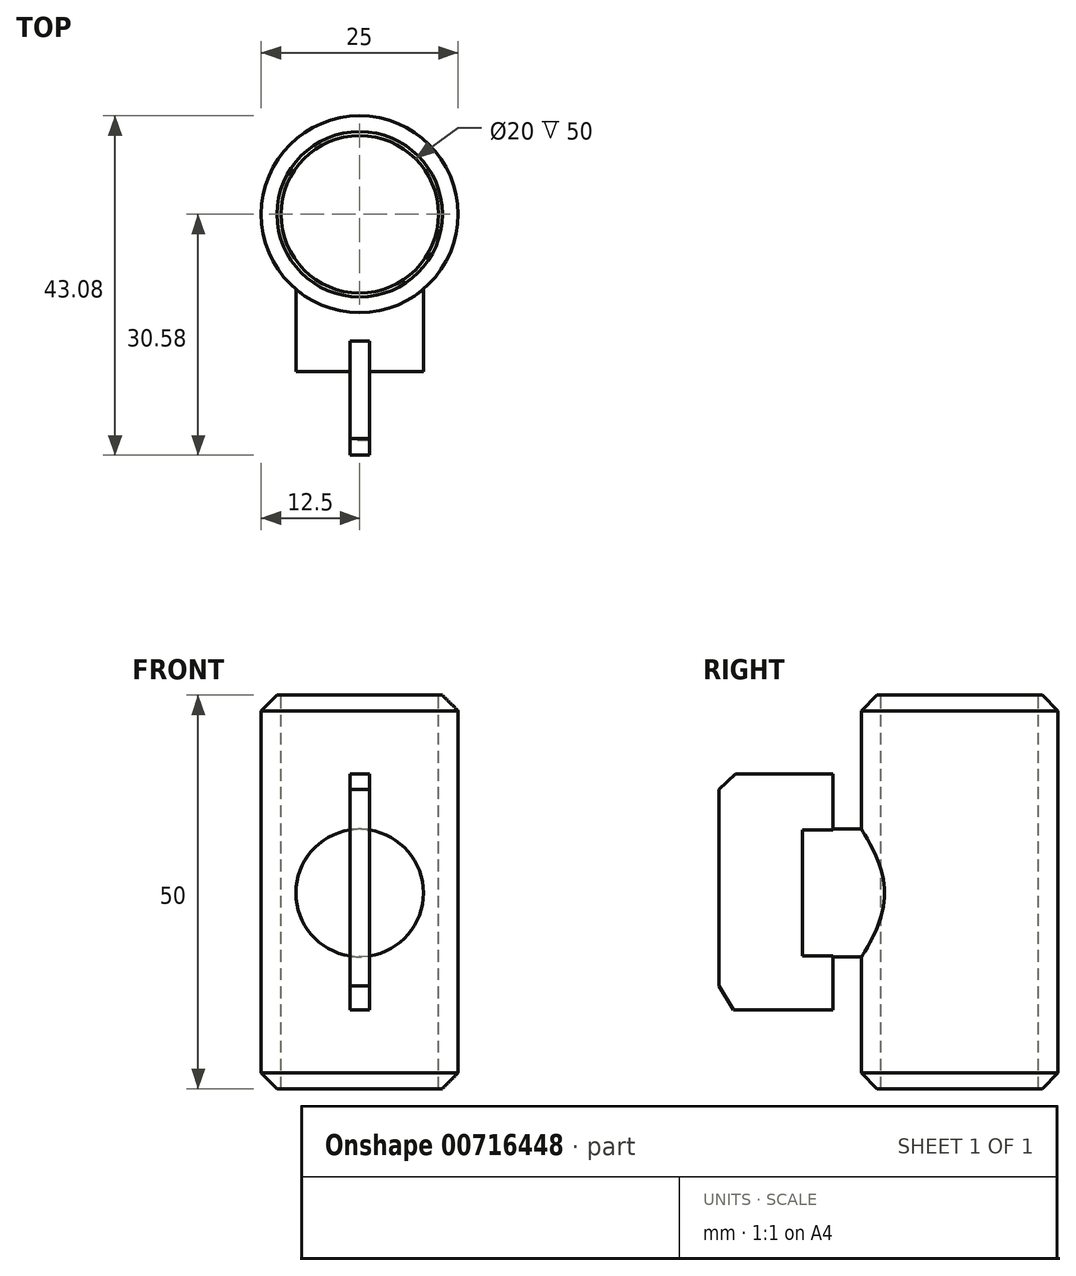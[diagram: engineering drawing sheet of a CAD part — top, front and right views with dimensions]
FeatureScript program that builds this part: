
annotation { "Feature Type Name" : "Feature", "Feature Type Description" : "" }
export const myFeature = defineFeature(function(context is Context, id is Id, definition is map)
    precondition{}
    {
        {
            var Q0;
            Q0=qCreatedBy(makeId("Top.planeOp"),FACE);
            var sketch = newSketch(context, id + "F0", { "sketchPlane" : qUnion([Q0])});
            skCircle(sketch, "E0", {"center": v(0, 0) * mm, "radius": 12.5 * mm});
            skSolve(sketch);
        }
        {
            var Q0;
            Q0=qSketchRegion(id+"F0",true);
            extrude(context, id + "F1", {"entities" : qUnion([Q0]), "depth" : 50 * mm, "offsetDistance" : 25 * mm});
        }
        {
            var Q0;
            Q0=makeQuery(id+"F1.opExtrude","CAP_EDGE",EDGE,{"disambiguationData":[OSD([sQuery(id+"F0.wireOp",EDGE,"E0")])],"isStart":false});
            var Q1;
            Q1=makeQuery(id+"F1.opExtrude","CAP_EDGE",EDGE,{"disambiguationData":[OSD([sQuery(id+"F0.wireOp",EDGE,"E0")])],"isStart":true});
            chamfer(context, id + "F2", {"entities" : qUnion([Q0, Q1]), "width" : 2 * mm, "tangentPropagation" : true});
        }
        {
            var Q0;
            Q0=qCreatedBy(makeId("Front.planeOp"),FACE);
            var sketch = newSketch(context, id + "F3", { "sketchPlane" : qUnion([Q0])});
            skCircle(sketch, "E1", {"center": v(0, 24.86) * mm, "radius": 8.1 * mm});
            skSolve(sketch);
        }
        {
            var Q0;
            Q0=qSketchRegion(id+"F3",true);
            extrude(context, id + "F4", {"entities" : qUnion([Q0]), "operationType" : NewBodyOperationType.ADD, "depth" : 20 * mm, "offsetDistance" : 25 * mm});
        }
        {
            var Q0;
            Q0=makeQuery(id+"F1.opExtrude","CAP_FACE",FACE,{"disambiguationData":[OSD([sQuery(id+"F0.wireOp",EDGE,"E0")])],"isStart":false});
            var sketch = newSketch(context, id + "F5", { "sketchPlane" : qUnion([Q0])});
            skCircle(sketch, "E2", {"center": v(0, 0) * mm, "radius": 10 * mm});
            skSolve(sketch);
        }
        {
            var Q0;
            Q0=qSketchRegion(id+"F5",true);
            extrude(context, id + "F6", {"entities" : qUnion([Q0]), "operationType" : NewBodyOperationType.REMOVE, "endBound" : BoundingType.THROUGH_ALL, "oppositeDirection" : true, "depth" : 25 * mm, "offsetDistance" : 25 * mm});
        }
        {
            var Q0;
            Q0=qCreatedBy(makeId("Right.planeOp"),FACE);
            var sketch = newSketch(context, id + "F7", { "sketchPlane" : qUnion([Q0])});
            skLineSegment(sketch, "E3.bottom", {"start": v(-28.47, 40) * mm, "end": v(-16.11, 40) * mm});
            skLineSegment(sketch, "E3.top", {"start": v(-28.74, 10) * mm, "end": v(-16.11, 10) * mm});
            skLineSegment(sketch, "E3.left", {"start": v(-30.58, 38) * mm, "end": v(-30.58, 13.06) * mm});
            skLineSegment(sketch, "E3.right", {"start": v(-16.11, 40) * mm, "end": v(-16.11, 10) * mm});
            skLineSegment(sketch, "E4", {"start": v(-28.47, 40) * mm, "end": v(-30.58, 38) * mm});
            skLineSegment(sketch, "E5", {"start": v(-30.58, 13.06) * mm, "end": v(-28.74, 10) * mm});
            skSolve(sketch);
        }
        {
            var Q0;
            Q0 = qSketchRegion(id + "F7", true);
            extrude(context, id + "F8", {"entities" : qUnion([Q0]), "operationType" : NewBodyOperationType.ADD, "depth" : 2.5 * mm, "offsetDistance" : 25 * mm, "symmetric" : true});
        }
    });
